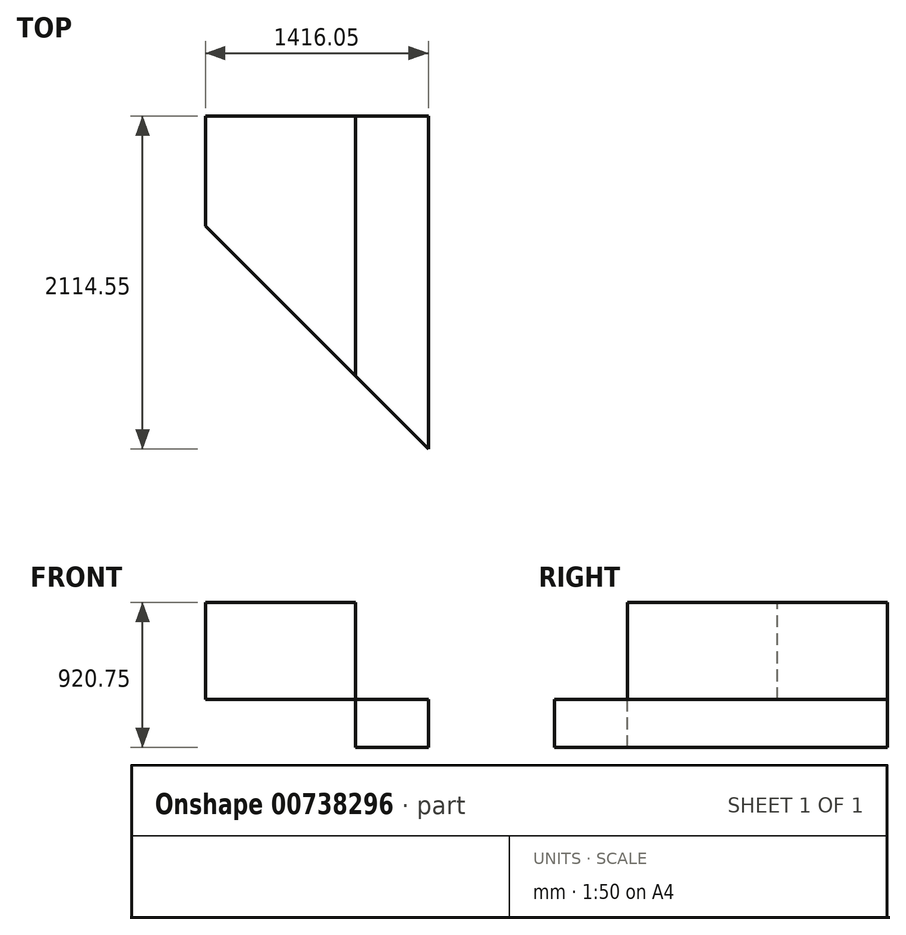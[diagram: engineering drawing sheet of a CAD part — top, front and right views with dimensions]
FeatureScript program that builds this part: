
annotation { "Feature Type Name" : "Feature", "Feature Type Description" : "" }
export const myFeature = defineFeature(function(context is Context, id is Id, definition is map)
    precondition{}
    {
        {
            var Q0;
            Q0=qCreatedBy(makeId("Front.planeOp"),FACE);
            var sketch = newSketch(context, id + "F0", { "sketchPlane" : qUnion([Q0])});
            skLineSegment(sketch, "E0.bottom", {"start": v(237.78, 171.63) * mm, "end": v(-225.77, 171.63) * mm});
            skLineSegment(sketch, "E0.top", {"start": v(237.78, -133.17) * mm, "end": v(-225.77, -133.17) * mm});
            skLineSegment(sketch, "E0.left", {"start": v(237.78, 171.63) * mm, "end": v(237.78, -133.17) * mm});
            skLineSegment(sketch, "E0.right", {"start": v(-225.77, 171.63) * mm, "end": v(-225.77, -133.17) * mm});
            skPoint(sketch, "E0.middle", {"position": v(6, 19.23) * mm});
            skSolve(sketch);
        }
        {
            var Q0;
            Q0=makeQuery(id+"F0.imprint","IMPRINT",FACE,{"disambiguationData":[TD([[makeQuery(id+"F0.imprint","IMPRINT",EDGE,{"derivedFrom":sQuery(id+"F0.wireOp",EDGE,"E0.bottom")}),1.0]])]});
            var sketch = newSketch(context, id + "F1", { "sketchPlane" : qUnion([Q0])});
            skLineSegment(sketch, "E1.bottom", {"start": v(-225.77, 171.63) * mm, "end": v(-1178.27, 171.63) * mm});
            skLineSegment(sketch, "E1.top", {"start": v(-225.77, 787.58) * mm, "end": v(-1178.27, 787.58) * mm});
            skLineSegment(sketch, "E1.left", {"start": v(-225.77, 171.63) * mm, "end": v(-225.77, 787.58) * mm});
            skLineSegment(sketch, "E1.right", {"start": v(-1178.27, 171.63) * mm, "end": v(-1178.27, 787.58) * mm});
            skSolve(sketch);
        }
        {
            var Q0;
            Q0=makeQuery(id+"F1.imprint","IMPRINT",FACE,{"disambiguationData":[TD([[makeQuery(id+"F1.imprint","IMPRINT",EDGE,{"derivedFrom":makeQuery(id+"F0.imprint","IMPRINT",EDGE,{"derivedFrom":sQuery(id+"F0.wireOp",EDGE,"E0.bottom")})}),1.0]])]});
            extrude(context, id + "F2", {"entities" : qUnion([Q0]), "depth" : 2120.9 * mm, "offsetDistance" : 25.4 * mm});
        }
        {
            var Q0;
            Q0 = qSketchRegion(id + "F1", true);
            extrude(context, id + "F3", {"entities" : qUnion([Q0]), "depth" : 1651 * mm, "offsetDistance" : 25.4 * mm});
        }
        {
            var Q0;
            Q0=makeQuery(id+"F2.opExtrude","CAP_EDGE",EDGE,{"disambiguationData":[OSD([sQuery(id+"F0.wireOp",EDGE,"E0.right")])],"isStart":false});
            chamfer(context, id + "F4", {"entities" : qUnion([Q0]), "width" : 469.9 * mm, "tangentPropagation" : true});
        }
        {
            var Q0;
            Q0=makeQuery(id+"F3.opExtrude","CAP_EDGE",EDGE,{"disambiguationData":[OSD([sQuery(id+"F1.wireOp",EDGE,"E1.right")])],"isStart":false});
            chamfer(context, id + "F5", {"entities" : qUnion([Q0]), "width" : 952.5 * mm, "tangentPropagation" : true});
        }
    });
